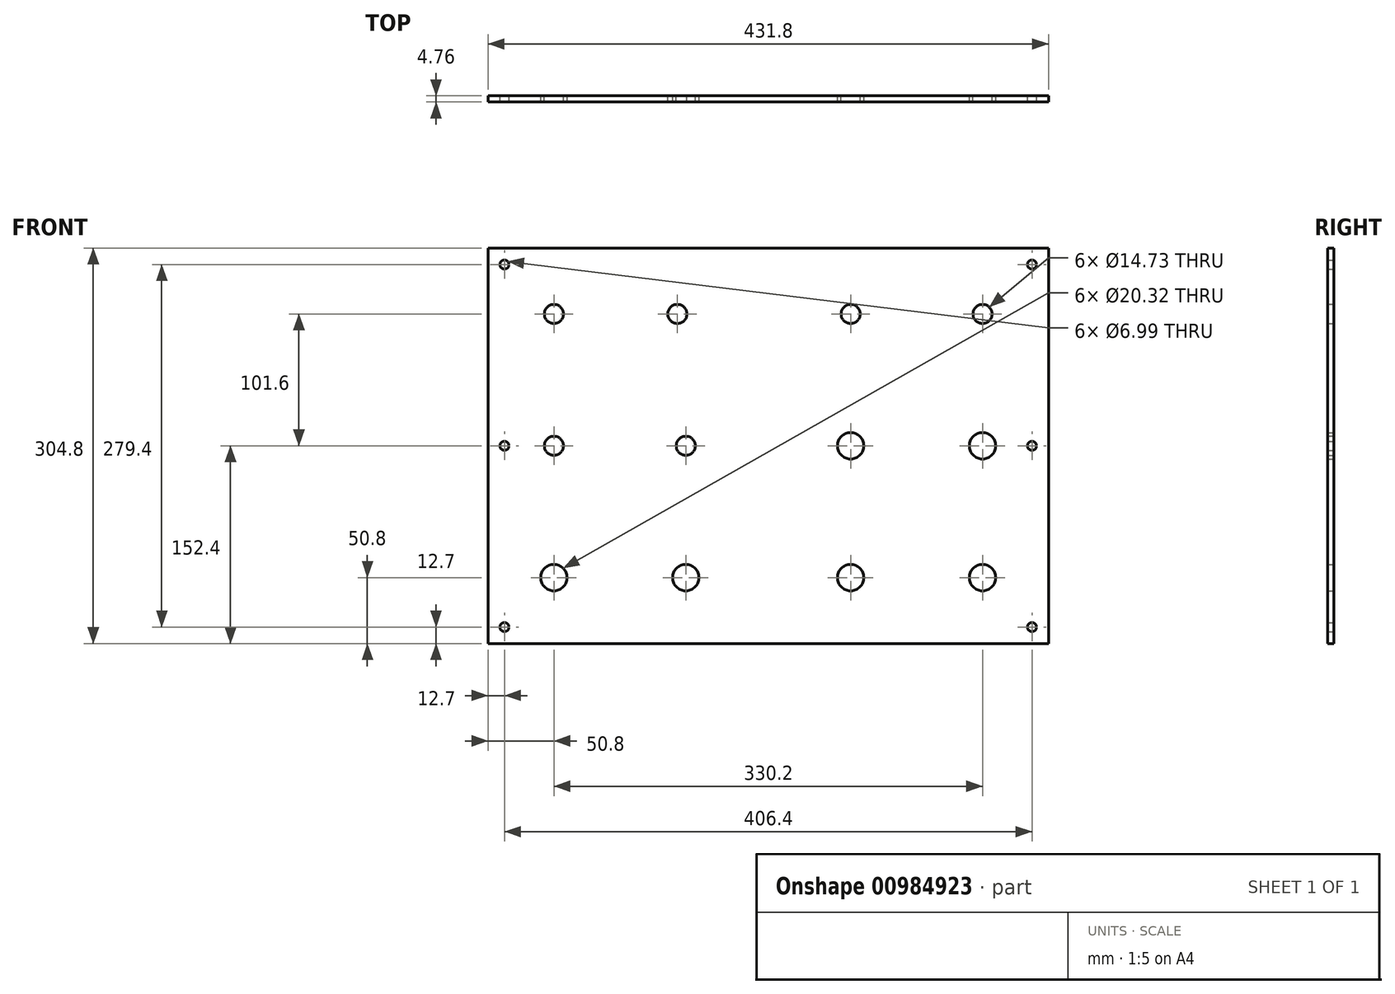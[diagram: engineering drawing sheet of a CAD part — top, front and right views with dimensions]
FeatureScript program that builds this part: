
annotation { "Feature Type Name" : "Feature", "Feature Type Description" : "" }
export const myFeature = defineFeature(function(context is Context, id is Id, definition is map)
    precondition{}
    {
        {
            var Q0;
            Q0=qCreatedBy(makeId("Front.planeOp"),FACE);
            var sketch = newSketch(context, id + "F0", { "sketchPlane" : qUnion([Q0])});
            skLineSegment(sketch, "E0.bottom", {"start": v(215.9, 152.4) * mm, "end": v(-215.9, 152.4) * mm});
            skLineSegment(sketch, "E0.top", {"start": v(215.9, -152.4) * mm, "end": v(-215.9, -152.4) * mm});
            skLineSegment(sketch, "E0.left", {"start": v(215.9, 152.4) * mm, "end": v(215.9, -152.4) * mm});
            skLineSegment(sketch, "E0.right", {"start": v(-215.9, 152.4) * mm, "end": v(-215.9, -152.4) * mm});
            skPoint(sketch, "E0.middle", {"position": v(0, 0) * mm});
            skCircle(sketch, "E1", {"center": v(-203.2, 139.7) * mm, "radius": 3.5 * mm});
            skCircle(sketch, "E2", {"center": v(-203.2, 0) * mm, "radius": 3.5 * mm});
            skCircle(sketch, "E3", {"center": v(-203.2, -139.7) * mm, "radius": 3.5 * mm});
            skCircle(sketch, "E4", {"center": v(203.2, 139.7) * mm, "radius": 3.5 * mm});
            skCircle(sketch, "E5", {"center": v(203.2, 0) * mm, "radius": 3.5 * mm});
            skCircle(sketch, "E6", {"center": v(203.2, -139.7) * mm, "radius": 3.5 * mm});
            skCircle(sketch, "E7", {"center": v(-165.1, -101.6) * mm, "radius": 10.16 * mm});
            skCircle(sketch, "E8", {"center": v(-63.5, -101.6) * mm, "radius": 10.16 * mm});
            skCircle(sketch, "E9", {"center": v(63.5, -101.6) * mm, "radius": 10.16 * mm});
            skCircle(sketch, "E10", {"center": v(165.1, -101.6) * mm, "radius": 10.16 * mm});
            skCircle(sketch, "E11", {"center": v(-165.1, 0) * mm, "radius": 7.37 * mm});
            skCircle(sketch, "E12", {"center": v(-63.5, 0) * mm, "radius": 7.37 * mm});
            skCircle(sketch, "E13", {"center": v(-165.1, 101.6) * mm, "radius": 7.37 * mm});
            skCircle(sketch, "E14", {"center": v(-69.99, 101.6) * mm, "radius": 7.37 * mm});
            skCircle(sketch, "E15", {"center": v(63.5, 0) * mm, "radius": 10.16 * mm});
            skCircle(sketch, "E16", {"center": v(165.1, 0) * mm, "radius": 10.16 * mm});
            skCircle(sketch, "E17", {"center": v(63.5, 101.6) * mm, "radius": 7.37 * mm});
            skCircle(sketch, "E18", {"center": v(165.1, 101.6) * mm, "radius": 7.37 * mm});
            skSolve(sketch);
        }
        {
            var Q0;
            Q0 = qSketchRegion(id + "F0", true);
            extrude(context, id + "F1", {"entities" : qUnion([Q0]), "depth" : 4.76 * mm, "offsetDistance" : 25.4 * mm});
        }
    });
